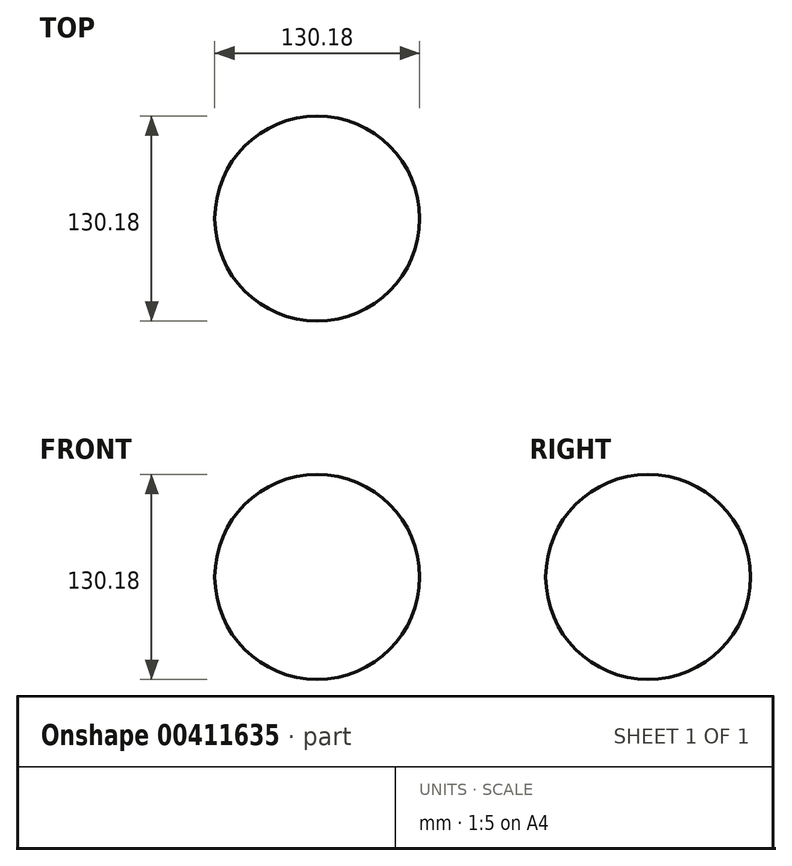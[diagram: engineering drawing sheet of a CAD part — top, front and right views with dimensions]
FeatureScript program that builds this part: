
annotation { "Feature Type Name" : "Feature", "Feature Type Description" : "" }
export const myFeature = defineFeature(function(context is Context, id is Id, definition is map)
    precondition{}
    {
        {
            var Q0;
            Q0=qCreatedBy(makeId("Front.planeOp"),FACE);
            var sketch = newSketch(context, id + "F0", { "sketchPlane" : qUnion([Q0])});
            skLineSegment(sketch, "E0", {"start": v(0, 58.83) * mm, "end": v(0, -71.35) * mm});
            skArc(sketch, "E1", {"start": v(0, -71.35) * mm, "mid": v(65.09, -6.26) * mm, "end": v(0, 58.83) * mm});
            skSolve(sketch);
        }
        {
            var Q0;
            Q0=makeQuery(id+"F0.imprint","IMPRINT",FACE,{"disambiguationData":[TD([[makeQuery(id+"F0.imprint","IMPRINT",EDGE,{"derivedFrom":sQuery(id+"F0.wireOp",EDGE,"E0")}),1.0]])]});
            var Q1;
            Q1=sQuery(id+"F0.wireOp",EDGE,"E0");
            revolve(context, id + "F1", {"entities" : qUnion([Q0]), "axis" : qUnion([Q1]), "revolveType" : RevolveType.FULL});
        }
    });
